# Revit family: Faucet-Lavatory-KOHLER-Avid-K-97345_1
name_source: partatom
category: Plumbing Fixtures
revit_build: Autodesk Revit 2017 (Build: 20160225_1515(x64)
units: mm (PartAtom-declared; Revit-internal decimal feet)

## family parameters
Cut with Voids When Loaded = No
Host = Face
OmniClass Number = 23.31.11.00
OmniClass Title = Faucets
Part Type = Normal
Room Calculation Point = No
Round Connector Dimension = Use Diameter
Shared = No

## types (2) — shared parameters
ADA Compliant = Yes
Assembly Code = D2010
CW Connection = Yes
Cold Water Inlet = Cold Water Inlet
Date Modified = 04/15/2020
Default Elevation = 36"
Description = 1.2 gpm single-handle faucet
Drain Included = Yes
Flow Rate = 1 GPM
HW Connection = Yes
Height = 5 7/16"
Hot Water Inlet = Hot Water Inlet
Length = 5 7/8"
Manufacturer = KOHLER Co.
Master Format 2014 = 22 41 39
Master Format 2014 Name = Residential Faucets, Supplies, and Trim
Material = Premium Metal Construction
Pressure = 60.00 psi
Product Documentation Link = https://www.us.kohler.com
Product Name = Avid
Product Page URL = http://www.us.kohler.com
Spout Reach = 5 7/8"
URL = https://www.us.kohler.com
Vent Connection = No
Waste Connection = No
Waste Water Outlet = Waste Water Outlet
WaterSense Certified = Yes
Width = 2"

## per-type parameters (varying)
| type | Finish | Model | Type |
| CP -  Polished Chrome | Kohler-Metal-CP-Polished_Chrome | K-97345-4-CP | 1 |
| BN - Vibrant Brushed Nickel | Kohler-Metal-BN-Vibrant_Brushed_Nickel | K-97345-4-BN | 2 |

## geometry (parser evidence)
native form markers: Sweep x6
no freeform markers — native parametric forms only
